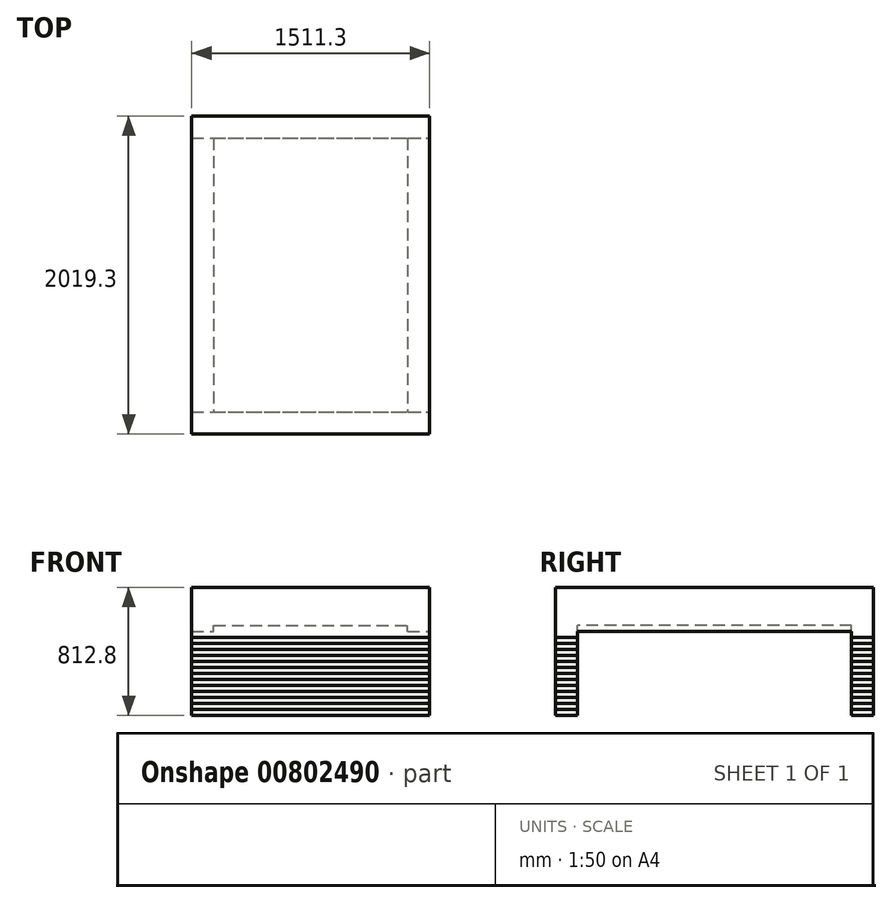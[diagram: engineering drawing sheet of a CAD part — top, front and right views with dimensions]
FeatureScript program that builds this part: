
annotation { "Feature Type Name" : "Feature", "Feature Type Description" : "" }
export const myFeature = defineFeature(function(context is Context, id is Id, definition is map)
    precondition{}
    {
        {
            var Q0;
            Q0=qCreatedBy(makeId("Top.planeOp"),FACE);
            var sketch = newSketch(context, id + "F0", { "sketchPlane" : qUnion([Q0])});
            skLineSegment(sketch, "E0.bottom", {"start": v(755.65, -1009.65) * mm, "end": v(-755.65, -1009.65) * mm});
            skLineSegment(sketch, "E0.top", {"start": v(755.65, 1009.65) * mm, "end": v(-755.65, 1009.65) * mm});
            skLineSegment(sketch, "E0.left", {"start": v(755.65, -1009.65) * mm, "end": v(755.65, 1009.65) * mm});
            skLineSegment(sketch, "E0.right", {"start": v(-755.65, -1009.65) * mm, "end": v(-755.65, 1009.65) * mm});
            skPoint(sketch, "E0.middle", {"position": v(0, 0) * mm});
            skSolve(sketch);
        }
        {
            var Q0;
            Q0 = qSketchRegion(id + "F0", true);
            extrude(context, id + "F1", {"entities" : qUnion([Q0]), "depth" : 241.3 * mm, "offsetDistance" : 25.4 * mm});
        }
        {
            var Q0;
            Q0=makeQuery(id+"F1.opExtrude","CAP_FACE",FACE,{"disambiguationData":[OSD([sQuery(id+"F0.wireOp",EDGE,"E0.bottom"),sQuery(id+"F0.wireOp",EDGE,"E0.top"),sQuery(id+"F0.wireOp",EDGE,"E0.left"),sQuery(id+"F0.wireOp",EDGE,"E0.right")])],"isStart":true});
            cPlane(context, id + "F2", {"entities" : qUnion([Q0]), "cplaneType" : CPlaneType.OFFSET, "offset" : 38.1 * mm, "width" : 152.4 * mm, "height" : 152.4 * mm});
        }
        {
            var Q0;
            Q0=qCreatedBy(id+"F2.planeOp",FACE);
            var sketch = newSketch(context, id + "F3", { "sketchPlane" : qUnion([Q0])});
            skLineSegment(sketch, "E1.bottom", {"start": v(755.65, 1009.65) * mm, "end": v(615.95, 1009.65) * mm});
            skLineSegment(sketch, "E1.top", {"start": v(755.65, 869.95) * mm, "end": v(615.95, 869.95) * mm});
            skLineSegment(sketch, "E1.left", {"start": v(755.65, 1009.65) * mm, "end": v(755.65, 869.95) * mm});
            skLineSegment(sketch, "E1.right", {"start": v(615.95, 1009.65) * mm, "end": v(615.95, 869.95) * mm});
            skLineSegment(sketch, "E2.MirrorCS", {"start": v(-755.65, 1009.65) * mm, "end": v(-615.95, 1009.65) * mm});
            skLineSegment(sketch, "E3.MirrorCS", {"start": v(-615.95, 1009.65) * mm, "end": v(-615.95, 869.95) * mm});
            skLineSegment(sketch, "E4.MirrorCS", {"start": v(-755.65, 869.95) * mm, "end": v(-615.95, 869.95) * mm});
            skLineSegment(sketch, "E5.MirrorCS", {"start": v(-755.65, 1009.65) * mm, "end": v(-755.65, 869.95) * mm});
            skLineSegment(sketch, "E6.MirrorCS", {"start": v(755.65, -1009.65) * mm, "end": v(615.95, -1009.65) * mm});
            skLineSegment(sketch, "E7.MirrorCS", {"start": v(615.95, -1009.65) * mm, "end": v(615.95, -869.95) * mm});
            skLineSegment(sketch, "E8.MirrorCS", {"start": v(755.65, -869.95) * mm, "end": v(615.95, -869.95) * mm});
            skLineSegment(sketch, "E9.MirrorCS", {"start": v(755.65, -1009.65) * mm, "end": v(755.65, -869.95) * mm});
            skLineSegment(sketch, "E10.MirrorCS", {"start": v(-755.65, -1009.65) * mm, "end": v(-615.95, -1009.65) * mm});
            skLineSegment(sketch, "E11.MirrorCS", {"start": v(-615.95, -1009.65) * mm, "end": v(-615.95, -869.95) * mm});
            skLineSegment(sketch, "E12.MirrorCS", {"start": v(-755.65, -869.95) * mm, "end": v(-615.95, -869.95) * mm});
            skLineSegment(sketch, "E13.MirrorCS", {"start": v(-755.65, -1009.65) * mm, "end": v(-755.65, -869.95) * mm});
            skSolve(sketch);
        }
        {
            var Q0;
            Q0=makeQuery(id+"F7quM40viauXstX_1.opExtrude","CAP_FACE",FACE,{"disambiguationData":[OSD([sQuery(id+"F3.wireOp",EDGE,"E2.MirrorCS"),sQuery(id+"F3.wireOp",EDGE,"E3.MirrorCS"),sQuery(id+"F3.wireOp",EDGE,"E4.MirrorCS"),sQuery(id+"F3.wireOp",EDGE,"E5.MirrorCS")])],"isStart":true});
            var sketch = newSketch(context, id + "F4", { "sketchPlane" : qUnion([Q0])});
            skLineSegment(sketch, "E14.bottom", {"start": v(-755.65, -1009.65) * mm, "end": v(755.65, -1009.65) * mm});
            skLineSegment(sketch, "E14.top", {"start": v(-755.65, 1009.65) * mm, "end": v(755.65, 1009.65) * mm});
            skLineSegment(sketch, "E14.left", {"start": v(-755.65, -1009.65) * mm, "end": v(-755.65, 1009.65) * mm});
            skLineSegment(sketch, "E14.right", {"start": v(755.65, -1009.65) * mm, "end": v(755.65, 1009.65) * mm});
            skLineSegment(sketch, "E15.0", {"start": v(-615.95, 869.95) * mm, "end": v(615.95, 869.95) * mm});
            skLineSegment(sketch, "E15.1", {"start": v(-615.95, -869.95) * mm, "end": v(-615.95, 869.95) * mm});
            skLineSegment(sketch, "E15.2", {"start": v(-615.95, -869.95) * mm, "end": v(615.95, -869.95) * mm});
            skLineSegment(sketch, "E15.3", {"start": v(615.95, -869.95) * mm, "end": v(615.95, 869.95) * mm});
            skSolve(sketch);
        }
        {
            var Q0;
            Q0=makeQuery(id+"F1.opExtrude","CAP_FACE",FACE,{"disambiguationData":[OSD([sQuery(id+"F0.wireOp",EDGE,"E0.bottom"),sQuery(id+"F0.wireOp",EDGE,"E0.top"),sQuery(id+"F0.wireOp",EDGE,"E0.left"),sQuery(id+"F0.wireOp",EDGE,"E0.right")])],"isStart":true});
            var sketch = newSketch(context, id + "F5", { "sketchPlane" : qUnion([Q0])});
            skLineSegment(sketch, "E16.bottom", {"start": v(-755.65, 1009.65) * mm, "end": v(755.65, 1009.65) * mm});
            skLineSegment(sketch, "E16.top", {"start": v(-755.65, 869.95) * mm, "end": v(755.65, 869.95) * mm});
            skLineSegment(sketch, "E16.left", {"start": v(-755.65, 1009.65) * mm, "end": v(-755.65, 869.95) * mm});
            skLineSegment(sketch, "E16.right", {"start": v(755.65, 1009.65) * mm, "end": v(755.65, 869.95) * mm});
            skLineSegment(sketch, "E17.bottom", {"start": v(755.65, 0) * mm, "end": v(615.95, 0) * mm});
            skLineSegment(sketch, "E17.top", {"start": v(755.65, 869.95) * mm, "end": v(615.95, 869.95) * mm});
            skLineSegment(sketch, "E17.left", {"start": v(755.65, 0) * mm, "end": v(755.65, 869.95) * mm});
            skLineSegment(sketch, "E17.right", {"start": v(615.95, 0) * mm, "end": v(615.95, 869.95) * mm});
            skLineSegment(sketch, "E18.bottom", {"start": v(-755.65, 0) * mm, "end": v(-615.95, 0) * mm});
            skLineSegment(sketch, "E18.top", {"start": v(-755.65, 869.95) * mm, "end": v(-615.95, 869.95) * mm});
            skLineSegment(sketch, "E18.left", {"start": v(-755.65, 0) * mm, "end": v(-755.65, 869.95) * mm});
            skLineSegment(sketch, "E18.right", {"start": v(-615.95, 0) * mm, "end": v(-615.95, 869.95) * mm});
            skSolve(sketch);
        }
        {
            var Q0;
            Q0 = qSketchRegion(id + "F5", true);
            extrude(context, id + "F6", {"entities" : qUnion([Q0]), "depth" : 38.1 * mm, "offsetDistance" : 25.4 * mm});
        }
        {
            var Q0;
            Q0=makeQuery(id+"F6.opExtrude","CAP_FACE",FACE,{"disambiguationData":[OSD([sQuery(id+"F5.wireOp",EDGE,"E16.bottom"),sQuery(id+"F5.wireOp",EDGE,"E16.top"),sQuery(id+"F5.wireOp",EDGE,"E16.left"),sQuery(id+"F5.wireOp",EDGE,"E16.right")])],"isStart":false});
            var sketch = newSketch(context, id + "F7", { "sketchPlane" : qUnion([Q0])});
            skLineSegment(sketch, "E19.bottom", {"start": v(-755.65, 1009.65) * mm, "end": v(755.65, 1009.65) * mm});
            skLineSegment(sketch, "E19.top", {"start": v(-755.65, 869.95) * mm, "end": v(755.65, 869.95) * mm});
            skLineSegment(sketch, "E19.left", {"start": v(-755.65, 1009.65) * mm, "end": v(-755.65, 869.95) * mm});
            skLineSegment(sketch, "E19.right", {"start": v(755.65, 1009.65) * mm, "end": v(755.65, 869.95) * mm});
            skSolve(sketch);
        }
        {
            var Q0;
            Q0 = qSketchRegion(id + "F7", true);
            extrude(context, id + "F8", {"entities" : qUnion([Q0]), "depth" : 38.1 * mm, "offsetDistance" : 25.4 * mm});
        }
        {
            var Q0;
            Q0=makeQuery(id+"F8.opExtrude","CAP_FACE",FACE,{"disambiguationData":[OSD([sQuery(id+"F7.wireOp",EDGE,"E19.bottom"),sQuery(id+"F7.wireOp",EDGE,"E19.top"),sQuery(id+"F7.wireOp",EDGE,"E19.left"),sQuery(id+"F7.wireOp",EDGE,"E19.right")])],"isStart":false});
            var sketch = newSketch(context, id + "F9", { "sketchPlane" : qUnion([Q0])});
            skLineSegment(sketch, "E20.bottom", {"start": v(-755.65, 1009.65) * mm, "end": v(755.65, 1009.65) * mm});
            skLineSegment(sketch, "E20.top", {"start": v(-755.65, 869.95) * mm, "end": v(755.65, 869.95) * mm});
            skLineSegment(sketch, "E20.left", {"start": v(-755.65, 1009.65) * mm, "end": v(-755.65, 869.95) * mm});
            skLineSegment(sketch, "E20.right", {"start": v(755.65, 1009.65) * mm, "end": v(755.65, 869.95) * mm});
            skSolve(sketch);
        }
        {
            var Q0;
            Q0 = qSketchRegion(id + "F9", true);
            extrude(context, id + "F10", {"entities" : qUnion([Q0]), "depth" : 38.1 * mm, "offsetDistance" : 25.4 * mm});
        }
        {
            var Q0;
            Q0=makeQuery(id+"F10.opExtrude","CAP_FACE",FACE,{"disambiguationData":[OSD([sQuery(id+"F9.wireOp",EDGE,"E20.bottom"),sQuery(id+"F9.wireOp",EDGE,"E20.top"),sQuery(id+"F9.wireOp",EDGE,"E20.left"),sQuery(id+"F9.wireOp",EDGE,"E20.right")])],"isStart":false});
            var sketch = newSketch(context, id + "F11", { "sketchPlane" : qUnion([Q0])});
            skLineSegment(sketch, "E21.bottom", {"start": v(-755.65, 1009.65) * mm, "end": v(755.65, 1009.65) * mm});
            skLineSegment(sketch, "E21.top", {"start": v(-755.65, 869.95) * mm, "end": v(755.65, 869.95) * mm});
            skLineSegment(sketch, "E21.left", {"start": v(-755.65, 1009.65) * mm, "end": v(-755.65, 869.95) * mm});
            skLineSegment(sketch, "E21.right", {"start": v(755.65, 1009.65) * mm, "end": v(755.65, 869.95) * mm});
            skSolve(sketch);
        }
        {
            var Q0;
            Q0 = qSketchRegion(id + "F11", true);
            extrude(context, id + "F12", {"entities" : qUnion([Q0]), "depth" : 38.1 * mm, "offsetDistance" : 25.4 * mm});
        }
        {
            var Q0;
            Q0=makeQuery(id+"F12.opExtrude","CAP_FACE",FACE,{"disambiguationData":[OSD([sQuery(id+"F11.wireOp",EDGE,"E21.bottom"),sQuery(id+"F11.wireOp",EDGE,"E21.top"),sQuery(id+"F11.wireOp",EDGE,"E21.left"),sQuery(id+"F11.wireOp",EDGE,"E21.right")])],"isStart":false});
            var sketch = newSketch(context, id + "F13", { "sketchPlane" : qUnion([Q0])});
            skLineSegment(sketch, "E22.bottom", {"start": v(-755.65, 1009.65) * mm, "end": v(755.65, 1009.65) * mm});
            skLineSegment(sketch, "E22.top", {"start": v(-755.65, 869.95) * mm, "end": v(755.65, 869.95) * mm});
            skLineSegment(sketch, "E22.left", {"start": v(-755.65, 1009.65) * mm, "end": v(-755.65, 869.95) * mm});
            skLineSegment(sketch, "E22.right", {"start": v(755.65, 1009.65) * mm, "end": v(755.65, 869.95) * mm});
            skSolve(sketch);
        }
        {
            var Q0;
            Q0 = qSketchRegion(id + "F13", true);
            extrude(context, id + "F14", {"entities" : qUnion([Q0]), "depth" : 38.1 * mm, "offsetDistance" : 25.4 * mm});
        }
        {
            var Q0;
            Q0=makeQuery(id+"F14.opExtrude","CAP_FACE",FACE,{"disambiguationData":[OSD([sQuery(id+"F13.wireOp",EDGE,"E22.bottom"),sQuery(id+"F13.wireOp",EDGE,"E22.top"),sQuery(id+"F13.wireOp",EDGE,"E22.left"),sQuery(id+"F13.wireOp",EDGE,"E22.right")])],"isStart":false});
            var sketch = newSketch(context, id + "F15", { "sketchPlane" : qUnion([Q0])});
            skLineSegment(sketch, "E23.bottom", {"start": v(-755.65, 1009.65) * mm, "end": v(755.65, 1009.65) * mm});
            skLineSegment(sketch, "E23.top", {"start": v(-755.65, 869.95) * mm, "end": v(755.65, 869.95) * mm});
            skLineSegment(sketch, "E23.left", {"start": v(-755.65, 1009.65) * mm, "end": v(-755.65, 869.95) * mm});
            skLineSegment(sketch, "E23.right", {"start": v(755.65, 1009.65) * mm, "end": v(755.65, 869.95) * mm});
            skSolve(sketch);
        }
        {
            var Q0;
            Q0 = qSketchRegion(id + "F15", true);
            extrude(context, id + "F16", {"entities" : qUnion([Q0]), "depth" : 38.1 * mm, "offsetDistance" : 25.4 * mm});
        }
        {
            var Q0;
            Q0=makeQuery(id+"F16.opExtrude","CAP_FACE",FACE,{"disambiguationData":[OSD([sQuery(id+"F15.wireOp",EDGE,"E23.bottom"),sQuery(id+"F15.wireOp",EDGE,"E23.top"),sQuery(id+"F15.wireOp",EDGE,"E23.left"),sQuery(id+"F15.wireOp",EDGE,"E23.right")])],"isStart":false});
            var sketch = newSketch(context, id + "F17", { "sketchPlane" : qUnion([Q0])});
            skLineSegment(sketch, "E24.bottom", {"start": v(-755.65, 1009.65) * mm, "end": v(755.65, 1009.65) * mm});
            skLineSegment(sketch, "E24.top", {"start": v(-755.65, 869.95) * mm, "end": v(755.65, 869.95) * mm});
            skLineSegment(sketch, "E24.left", {"start": v(-755.65, 1009.65) * mm, "end": v(-755.65, 869.95) * mm});
            skLineSegment(sketch, "E24.right", {"start": v(755.65, 1009.65) * mm, "end": v(755.65, 869.95) * mm});
            skSolve(sketch);
        }
        {
            var Q0;
            Q0 = qSketchRegion(id + "F17", true);
            extrude(context, id + "F18", {"entities" : qUnion([Q0]), "depth" : 38.1 * mm, "offsetDistance" : 25.4 * mm});
        }
        {
            var Q0;
            Q0=makeQuery(id+"F18.opExtrude","CAP_FACE",FACE,{"disambiguationData":[OSD([sQuery(id+"F17.wireOp",EDGE,"E24.bottom"),sQuery(id+"F17.wireOp",EDGE,"E24.top"),sQuery(id+"F17.wireOp",EDGE,"E24.left"),sQuery(id+"F17.wireOp",EDGE,"E24.right")])],"isStart":false});
            var sketch = newSketch(context, id + "F19", { "sketchPlane" : qUnion([Q0])});
            skLineSegment(sketch, "E25.bottom", {"start": v(-755.65, 1009.65) * mm, "end": v(755.65, 1009.65) * mm});
            skLineSegment(sketch, "E25.top", {"start": v(-755.65, 869.95) * mm, "end": v(755.65, 869.95) * mm});
            skLineSegment(sketch, "E25.left", {"start": v(-755.65, 1009.65) * mm, "end": v(-755.65, 869.95) * mm});
            skLineSegment(sketch, "E25.right", {"start": v(755.65, 1009.65) * mm, "end": v(755.65, 869.95) * mm});
            skSolve(sketch);
        }
        {
            var Q0;
            Q0 = qSketchRegion(id + "F19", true);
            extrude(context, id + "F20", {"entities" : qUnion([Q0]), "depth" : 38.1 * mm, "offsetDistance" : 25.4 * mm});
        }
        {
            var Q0;
            Q0=makeQuery(id+"F20.opExtrude","CAP_FACE",FACE,{"disambiguationData":[OSD([sQuery(id+"F19.wireOp",EDGE,"E25.bottom"),sQuery(id+"F19.wireOp",EDGE,"E25.top"),sQuery(id+"F19.wireOp",EDGE,"E25.left"),sQuery(id+"F19.wireOp",EDGE,"E25.right")])],"isStart":false});
            var sketch = newSketch(context, id + "F21", { "sketchPlane" : qUnion([Q0])});
            skLineSegment(sketch, "E26.bottom", {"start": v(-755.65, 1009.65) * mm, "end": v(755.65, 1009.65) * mm});
            skLineSegment(sketch, "E26.top", {"start": v(-755.65, 869.95) * mm, "end": v(755.65, 869.95) * mm});
            skLineSegment(sketch, "E26.left", {"start": v(-755.65, 1009.65) * mm, "end": v(-755.65, 869.95) * mm});
            skLineSegment(sketch, "E26.right", {"start": v(755.65, 1009.65) * mm, "end": v(755.65, 869.95) * mm});
            skSolve(sketch);
        }
        {
            var Q0;
            Q0 = qSketchRegion(id + "F21", true);
            extrude(context, id + "F22", {"entities" : qUnion([Q0]), "depth" : 38.1 * mm, "offsetDistance" : 25.4 * mm});
        }
        {
            var Q0;
            Q0=makeQuery(id+"F22.opExtrude","CAP_FACE",FACE,{"disambiguationData":[OSD([sQuery(id+"F21.wireOp",EDGE,"E26.bottom"),sQuery(id+"F21.wireOp",EDGE,"E26.top"),sQuery(id+"F21.wireOp",EDGE,"E26.left"),sQuery(id+"F21.wireOp",EDGE,"E26.right")])],"isStart":false});
            var sketch = newSketch(context, id + "F23", { "sketchPlane" : qUnion([Q0])});
            skLineSegment(sketch, "E27.bottom", {"start": v(-755.65, 1009.65) * mm, "end": v(755.65, 1009.65) * mm});
            skLineSegment(sketch, "E27.top", {"start": v(-755.65, 869.95) * mm, "end": v(755.65, 869.95) * mm});
            skLineSegment(sketch, "E27.left", {"start": v(-755.65, 1009.65) * mm, "end": v(-755.65, 869.95) * mm});
            skLineSegment(sketch, "E27.right", {"start": v(755.65, 1009.65) * mm, "end": v(755.65, 869.95) * mm});
            skSolve(sketch);
        }
        {
            var Q0;
            Q0 = qSketchRegion(id + "F23", true);
            extrude(context, id + "F24", {"entities" : qUnion([Q0]), "depth" : 38.1 * mm, "offsetDistance" : 25.4 * mm});
        }
        {
            var Q0;
            Q0=makeQuery(id+"F24.opExtrude","CAP_FACE",FACE,{"disambiguationData":[OSD([sQuery(id+"F23.wireOp",EDGE,"E27.bottom"),sQuery(id+"F23.wireOp",EDGE,"E27.top"),sQuery(id+"F23.wireOp",EDGE,"E27.left"),sQuery(id+"F23.wireOp",EDGE,"E27.right")])],"isStart":false});
            var sketch = newSketch(context, id + "F25", { "sketchPlane" : qUnion([Q0])});
            skLineSegment(sketch, "E28.bottom", {"start": v(-755.65, 1009.65) * mm, "end": v(755.65, 1009.65) * mm});
            skLineSegment(sketch, "E28.top", {"start": v(-755.65, 869.95) * mm, "end": v(755.65, 869.95) * mm});
            skLineSegment(sketch, "E28.left", {"start": v(-755.65, 1009.65) * mm, "end": v(-755.65, 869.95) * mm});
            skLineSegment(sketch, "E28.right", {"start": v(755.65, 1009.65) * mm, "end": v(755.65, 869.95) * mm});
            skSolve(sketch);
        }
        {
            var Q0;
            Q0 = qSketchRegion(id + "F25", true);
            extrude(context, id + "F26", {"entities" : qUnion([Q0]), "depth" : 38.1 * mm, "offsetDistance" : 25.4 * mm});
        }
        {
            var Q0;
            Q0=makeQuery(id+"F26.opExtrude","CAP_FACE",FACE,{"disambiguationData":[OSD([sQuery(id+"F25.wireOp",EDGE,"E28.bottom"),sQuery(id+"F25.wireOp",EDGE,"E28.top"),sQuery(id+"F25.wireOp",EDGE,"E28.left"),sQuery(id+"F25.wireOp",EDGE,"E28.right")])],"isStart":false});
            var sketch = newSketch(context, id + "F27", { "sketchPlane" : qUnion([Q0])});
            skLineSegment(sketch, "E29.bottom", {"start": v(-755.65, 1009.65) * mm, "end": v(755.65, 1009.65) * mm});
            skLineSegment(sketch, "E29.top", {"start": v(-755.65, 869.95) * mm, "end": v(755.65, 869.95) * mm});
            skLineSegment(sketch, "E29.left", {"start": v(-755.65, 1009.65) * mm, "end": v(-755.65, 869.95) * mm});
            skLineSegment(sketch, "E29.right", {"start": v(755.65, 1009.65) * mm, "end": v(755.65, 869.95) * mm});
            skSolve(sketch);
        }
        {
            var Q0;
            Q0 = qSketchRegion(id + "F27", true);
            extrude(context, id + "F28", {"entities" : qUnion([Q0]), "depth" : 38.1 * mm, "offsetDistance" : 25.4 * mm});
        }
        {
            var Q0;
            Q0=makeQuery(id+"F28.opExtrude","CAP_FACE",FACE,{"disambiguationData":[OSD([sQuery(id+"F27.wireOp",EDGE,"E29.bottom"),sQuery(id+"F27.wireOp",EDGE,"E29.top"),sQuery(id+"F27.wireOp",EDGE,"E29.left"),sQuery(id+"F27.wireOp",EDGE,"E29.right")])],"isStart":false});
            var sketch = newSketch(context, id + "F29", { "sketchPlane" : qUnion([Q0])});
            skLineSegment(sketch, "E30.bottom", {"start": v(-755.65, 1009.65) * mm, "end": v(755.65, 1009.65) * mm});
            skLineSegment(sketch, "E30.top", {"start": v(-755.65, 869.95) * mm, "end": v(755.65, 869.95) * mm});
            skLineSegment(sketch, "E30.left", {"start": v(-755.65, 1009.65) * mm, "end": v(-755.65, 869.95) * mm});
            skLineSegment(sketch, "E30.right", {"start": v(755.65, 1009.65) * mm, "end": v(755.65, 869.95) * mm});
            skSolve(sketch);
        }
        {
            var Q0;
            Q0 = qSketchRegion(id + "F29", true);
            extrude(context, id + "F30", {"entities" : qUnion([Q0]), "depth" : 38.1 * mm, "offsetDistance" : 25.4 * mm});
        }
        {
            var Q0;
            Q0=makeQuery(id+"F30.opExtrude","CAP_FACE",FACE,{"disambiguationData":[OSD([sQuery(id+"F29.wireOp",EDGE,"E30.bottom"),sQuery(id+"F29.wireOp",EDGE,"E30.top"),sQuery(id+"F29.wireOp",EDGE,"E30.left"),sQuery(id+"F29.wireOp",EDGE,"E30.right")])],"isStart":false});
            var sketch = newSketch(context, id + "F31", { "sketchPlane" : qUnion([Q0])});
            skLineSegment(sketch, "E31.bottom", {"start": v(-755.65, 1009.65) * mm, "end": v(755.65, 1009.65) * mm});
            skLineSegment(sketch, "E31.top", {"start": v(-755.65, 869.95) * mm, "end": v(755.65, 869.95) * mm});
            skLineSegment(sketch, "E31.left", {"start": v(-755.65, 1009.65) * mm, "end": v(-755.65, 869.95) * mm});
            skLineSegment(sketch, "E31.right", {"start": v(755.65, 1009.65) * mm, "end": v(755.65, 869.95) * mm});
            skSolve(sketch);
        }
        {
            var Q0;
            Q0 = qSketchRegion(id + "F31", true);
            extrude(context, id + "F32", {"entities" : qUnion([Q0]), "depth" : 38.1 * mm, "offsetDistance" : 25.4 * mm});
        }
        {
            var Q0;
            Q0=makeQuery(id+"F32.opExtrude","CAP_FACE",FACE,{"disambiguationData":[OSD([sQuery(id+"F31.wireOp",EDGE,"E31.bottom"),sQuery(id+"F31.wireOp",EDGE,"E31.top"),sQuery(id+"F31.wireOp",EDGE,"E31.left"),sQuery(id+"F31.wireOp",EDGE,"E31.right")])],"isStart":false});
            var sketch = newSketch(context, id + "F33", { "sketchPlane" : qUnion([Q0])});
            skLineSegment(sketch, "E32.bottom", {"start": v(-755.65, 1009.65) * mm, "end": v(755.65, 1009.65) * mm});
            skLineSegment(sketch, "E32.top", {"start": v(-755.65, 869.95) * mm, "end": v(755.65, 869.95) * mm});
            skLineSegment(sketch, "E32.left", {"start": v(-755.65, 1009.65) * mm, "end": v(-755.65, 869.95) * mm});
            skLineSegment(sketch, "E32.right", {"start": v(755.65, 1009.65) * mm, "end": v(755.65, 869.95) * mm});
            skSolve(sketch);
        }
        {
            var Q0;
            Q0 = qSketchRegion(id + "F33", true);
            extrude(context, id + "F34", {"entities" : qUnion([Q0]), "depth" : 38.1 * mm, "offsetDistance" : 25.4 * mm});
        }
        {
            var Q0;
            Q0=makeQuery(id+"F10.opExtrude","SWEPT_BODY",BODY,{"disambiguationData":[OSD([sQuery(id+"F9.wireOp",EDGE,"E20.bottom"),sQuery(id+"F9.wireOp",EDGE,"E20.top"),sQuery(id+"F9.wireOp",EDGE,"E20.left"),sQuery(id+"F9.wireOp",EDGE,"E20.right")])]});
            var Q1;
            Q1=makeQuery(id+"F12.opExtrude","SWEPT_BODY",BODY,{"disambiguationData":[OSD([sQuery(id+"F11.wireOp",EDGE,"E21.bottom"),sQuery(id+"F11.wireOp",EDGE,"E21.top"),sQuery(id+"F11.wireOp",EDGE,"E21.left"),sQuery(id+"F11.wireOp",EDGE,"E21.right")])]});
            var Q2;
            Q2=makeQuery(id+"F14.opExtrude","SWEPT_BODY",BODY,{"disambiguationData":[OSD([sQuery(id+"F13.wireOp",EDGE,"E22.bottom"),sQuery(id+"F13.wireOp",EDGE,"E22.top"),sQuery(id+"F13.wireOp",EDGE,"E22.left"),sQuery(id+"F13.wireOp",EDGE,"E22.right")])]});
            var Q3;
            Q3=makeQuery(id+"F16.opExtrude","SWEPT_BODY",BODY,{"disambiguationData":[OSD([sQuery(id+"F15.wireOp",EDGE,"E23.bottom"),sQuery(id+"F15.wireOp",EDGE,"E23.top"),sQuery(id+"F15.wireOp",EDGE,"E23.left"),sQuery(id+"F15.wireOp",EDGE,"E23.right")])]});
            var Q4;
            Q4=makeQuery(id+"F18.opExtrude","SWEPT_BODY",BODY,{"disambiguationData":[OSD([sQuery(id+"F17.wireOp",EDGE,"E24.bottom"),sQuery(id+"F17.wireOp",EDGE,"E24.top"),sQuery(id+"F17.wireOp",EDGE,"E24.left"),sQuery(id+"F17.wireOp",EDGE,"E24.right")])]});
            var Q5;
            Q5=makeQuery(id+"F20.opExtrude","SWEPT_BODY",BODY,{"disambiguationData":[OSD([sQuery(id+"F19.wireOp",EDGE,"E25.bottom"),sQuery(id+"F19.wireOp",EDGE,"E25.top"),sQuery(id+"F19.wireOp",EDGE,"E25.left"),sQuery(id+"F19.wireOp",EDGE,"E25.right")])]});
            var Q6;
            Q6=makeQuery(id+"F22.opExtrude","SWEPT_BODY",BODY,{"disambiguationData":[OSD([sQuery(id+"F21.wireOp",EDGE,"E26.bottom"),sQuery(id+"F21.wireOp",EDGE,"E26.top"),sQuery(id+"F21.wireOp",EDGE,"E26.left"),sQuery(id+"F21.wireOp",EDGE,"E26.right")])]});
            var Q7;
            Q7=makeQuery(id+"F24.opExtrude","SWEPT_BODY",BODY,{"disambiguationData":[OSD([sQuery(id+"F23.wireOp",EDGE,"E27.bottom"),sQuery(id+"F23.wireOp",EDGE,"E27.top"),sQuery(id+"F23.wireOp",EDGE,"E27.left"),sQuery(id+"F23.wireOp",EDGE,"E27.right")])]});
            var Q8;
            Q8=makeQuery(id+"F26.opExtrude","SWEPT_BODY",BODY,{"disambiguationData":[OSD([sQuery(id+"F25.wireOp",EDGE,"E28.bottom"),sQuery(id+"F25.wireOp",EDGE,"E28.top"),sQuery(id+"F25.wireOp",EDGE,"E28.left"),sQuery(id+"F25.wireOp",EDGE,"E28.right")])]});
            var Q9;
            Q9=makeQuery(id+"F28.opExtrude","SWEPT_BODY",BODY,{"disambiguationData":[OSD([sQuery(id+"F27.wireOp",EDGE,"E29.bottom"),sQuery(id+"F27.wireOp",EDGE,"E29.top"),sQuery(id+"F27.wireOp",EDGE,"E29.left"),sQuery(id+"F27.wireOp",EDGE,"E29.right")])]});
            var Q10;
            Q10=makeQuery(id+"F30.opExtrude","SWEPT_BODY",BODY,{"disambiguationData":[OSD([sQuery(id+"F29.wireOp",EDGE,"E30.bottom"),sQuery(id+"F29.wireOp",EDGE,"E30.top"),sQuery(id+"F29.wireOp",EDGE,"E30.left"),sQuery(id+"F29.wireOp",EDGE,"E30.right")])]});
            var Q11;
            Q11=makeQuery(id+"F32.opExtrude","SWEPT_BODY",BODY,{"disambiguationData":[OSD([sQuery(id+"F31.wireOp",EDGE,"E31.bottom"),sQuery(id+"F31.wireOp",EDGE,"E31.top"),sQuery(id+"F31.wireOp",EDGE,"E31.left"),sQuery(id+"F31.wireOp",EDGE,"E31.right")])]});
            var Q12;
            Q12=makeQuery(id+"F34.opExtrude","SWEPT_BODY",BODY,{"disambiguationData":[OSD([sQuery(id+"F33.wireOp",EDGE,"E32.bottom"),sQuery(id+"F33.wireOp",EDGE,"E32.top"),sQuery(id+"F33.wireOp",EDGE,"E32.left"),sQuery(id+"F33.wireOp",EDGE,"E32.right")])]});
            var Q13;
            Q13=makeQuery(id+"F8.opExtrude","SWEPT_BODY",BODY,{"disambiguationData":[OSD([sQuery(id+"F7.wireOp",EDGE,"E19.bottom"),sQuery(id+"F7.wireOp",EDGE,"E19.top"),sQuery(id+"F7.wireOp",EDGE,"E19.left"),sQuery(id+"F7.wireOp",EDGE,"E19.right")])]});
            var Q14;
            Q14=qCreatedBy(makeId("Front.planeOp"),FACE);
            mirror(context, id + "F35", {"entities" : qUnion([Q0, Q1, Q2, Q3, Q4, Q5, Q6, Q7, Q8, Q9, Q10, Q11, Q12, Q13]), "mirrorPlane" : qUnion([Q14])});
        }
        {
            var Q0;
            Q0=makeQuery(id+"F6.opExtrude","SWEPT_BODY",BODY,{"disambiguationData":[OSD([sQuery(id+"F5.wireOp",EDGE,"E16.bottom"),sQuery(id+"F5.wireOp",EDGE,"E16.top"),sQuery(id+"F5.wireOp",EDGE,"E16.left"),sQuery(id+"F5.wireOp",EDGE,"E16.right"),sQuery(id+"F5.wireOp",EDGE,"E17.bottom"),sQuery(id+"F5.wireOp",EDGE,"E17.left"),sQuery(id+"F5.wireOp",EDGE,"E17.right"),sQuery(id+"F5.wireOp",EDGE,"E18.bottom"),sQuery(id+"F5.wireOp",EDGE,"E18.left"),sQuery(id+"F5.wireOp",EDGE,"E18.right")])]});
            var Q1;
            Q1=qCreatedBy(makeId("Front.planeOp"),FACE);
            mirror(context, id + "F36", {"operationType" : NewBodyOperationType.ADD, "entities" : qUnion([Q0]), "mirrorPlane" : qUnion([Q1])});
        }
    });
